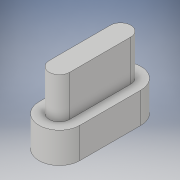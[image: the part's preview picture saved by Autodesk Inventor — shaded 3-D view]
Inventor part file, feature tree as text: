
AUTODESK INVENTOR PART (.ipt)
format: ipt  version: 2019 (Build 230136000, 136)  size: 111,104 bytes
history: native  units: mm
features: extrude x2, sketch x2
ambient origin geometry x8: Origin, YZ Plane, XZ Plane, XY Plane, X Axis, Y Axis, Z Axis, Center Point
bodies: Volumenkörper1 (feature_tree)
feature tree (4):
  extrude  "Extrusion1"  Depth=4.0mm
  extrude  "Extrusion2"  Depth=2.0mm
  sketch  "Skizze1"  dims[d0=4.0mm d1=6.0mm]
  sketch  "Skizze2"  dims[d2=3.0mm d3=0.0mm d4=2.0mm d5=6.0mm d6=1.0mm d7=0.0mm d8=4.0mm d9=0.0mm]
